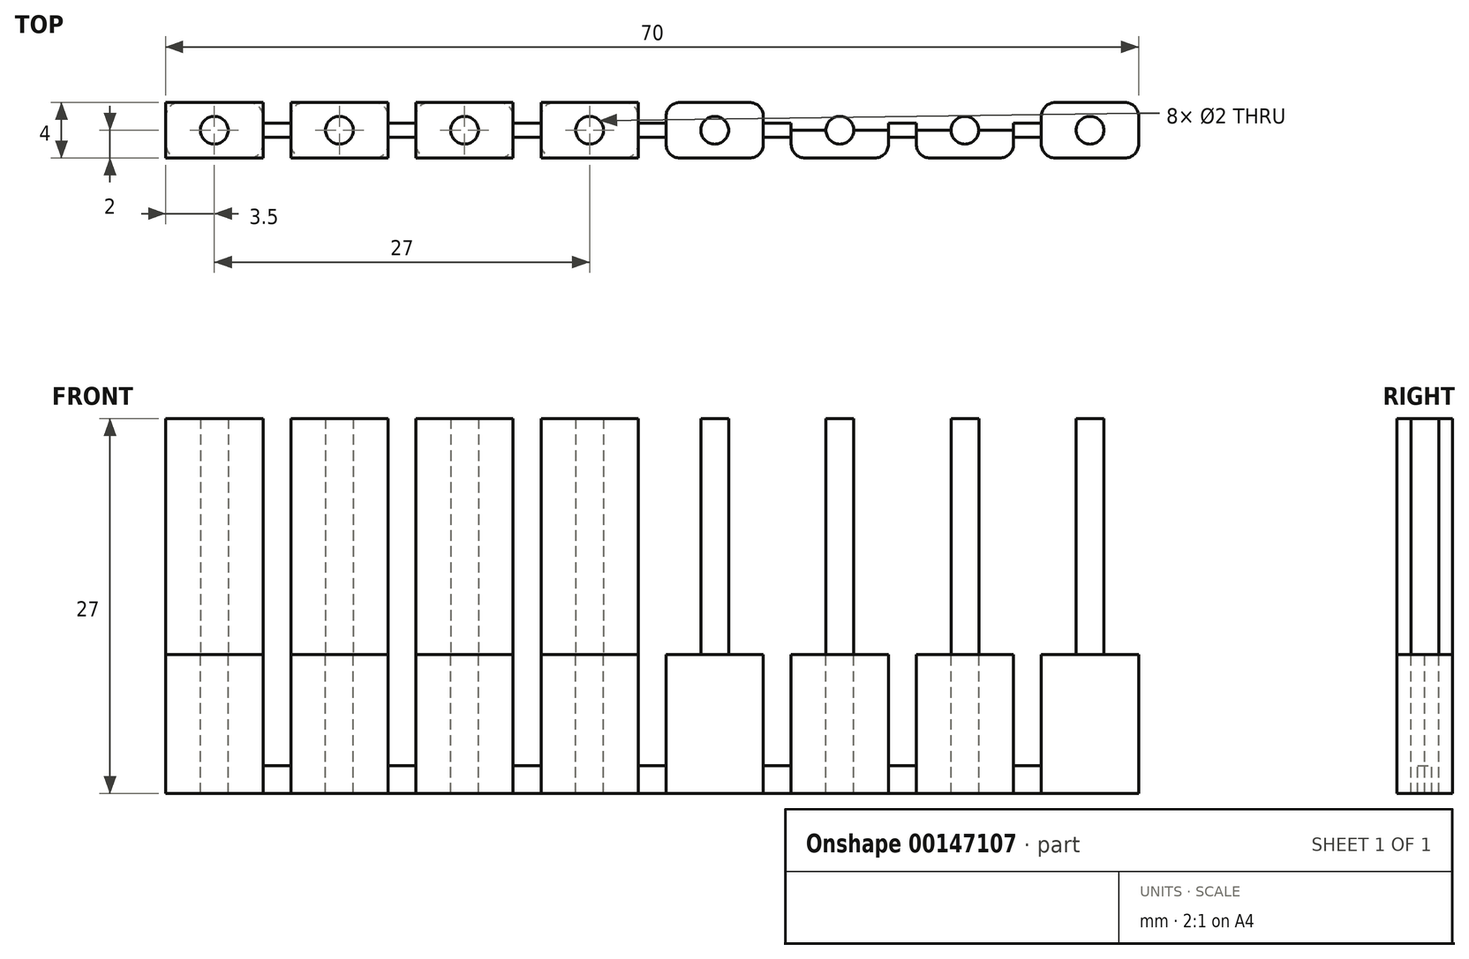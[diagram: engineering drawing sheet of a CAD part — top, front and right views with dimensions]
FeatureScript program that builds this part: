
annotation { "Feature Type Name" : "Feature", "Feature Type Description" : "" }
export const myFeature = defineFeature(function(context is Context, id is Id, definition is map)
    precondition{}
    {
        {
            var Q0;
            Q0=qCreatedBy(makeId("Top.planeOp"),FACE);
            var sketch = newSketch(context, id + "F0", { "sketchPlane" : qUnion([Q0])});
            skLineSegment(sketch, "E0.bottom", {"start": v(35, 2) * mm, "end": v(-35, 2) * mm});
            skLineSegment(sketch, "E0.top", {"start": v(35, -2) * mm, "end": v(-35, -2) * mm});
            skLineSegment(sketch, "E0.left", {"start": v(35, 2) * mm, "end": v(35, -2) * mm});
            skLineSegment(sketch, "E0.right", {"start": v(-35, 2) * mm, "end": v(-35, -2) * mm});
            skPoint(sketch, "E0.middle", {"position": v(0, 0) * mm});
            skLineSegment(sketch, "E1", {"start": v(0, 0) * mm, "end": v(4.5, 0) * mm});
            skLineSegment(sketch, "E2", {"start": v(4.5, 0) * mm, "end": v(13.5, 0) * mm});
            skLineSegment(sketch, "E3", {"start": v(13.5, 0) * mm, "end": v(22.5, 0) * mm});
            skLineSegment(sketch, "E4", {"start": v(22.5, 0) * mm, "end": v(31.5, 0) * mm});
            skCircle(sketch, "E5", {"center": v(4.5, 0) * mm, "radius": 1 * mm});
            skCircle(sketch, "E6", {"center": v(13.5, 0) * mm, "radius": 1 * mm});
            skCircle(sketch, "E7", {"center": v(22.5, 0) * mm, "radius": 1 * mm});
            skCircle(sketch, "E8", {"center": v(31.5, 0) * mm, "radius": 1 * mm});
            skLineSegment(sketch, "E9", {"start": v(0, 2) * mm, "end": v(8, 2) * mm});
            skLineSegment(sketch, "E10", {"start": v(8, 2) * mm, "end": v(10, 2) * mm});
            skLineSegment(sketch, "E11", {"start": v(10, 2) * mm, "end": v(17, 2) * mm});
            skLineSegment(sketch, "E12", {"start": v(17, 2) * mm, "end": v(19, 2) * mm});
            skLineSegment(sketch, "E13", {"start": v(19, 2) * mm, "end": v(26, 2) * mm});
            skLineSegment(sketch, "E14", {"start": v(26, 2) * mm, "end": v(28, 2) * mm});
            skLineSegment(sketch, "E15", {"start": v(8, 2) * mm, "end": v(8, 0.5) * mm});
            skLineSegment(sketch, "E16", {"start": v(8, 0.5) * mm, "end": v(10, 0.5) * mm});
            skLineSegment(sketch, "E17", {"start": v(10, 0.5) * mm, "end": v(10, 2) * mm});
            skLineSegment(sketch, "E18", {"start": v(17, 2) * mm, "end": v(17, 0.5) * mm});
            skLineSegment(sketch, "E19", {"start": v(17, 0.5) * mm, "end": v(19, 0.5) * mm});
            skLineSegment(sketch, "E20", {"start": v(19, 0.5) * mm, "end": v(19, 2) * mm});
            skLineSegment(sketch, "E21", {"start": v(26, 2) * mm, "end": v(26, 0.5) * mm});
            skLineSegment(sketch, "E22", {"start": v(26, 0.5) * mm, "end": v(28, 0.5) * mm});
            skLineSegment(sketch, "E23", {"start": v(28, 0.5) * mm, "end": v(28, 2) * mm});
            skLineSegment(sketch, "E24.MirrorCS", {"start": v(8, -0.5) * mm, "end": v(10, -0.5) * mm});
            skLineSegment(sketch, "E25.MirrorCS", {"start": v(8, -2) * mm, "end": v(8, -0.5) * mm});
            skLineSegment(sketch, "E26.MirrorCS", {"start": v(10, -0.5) * mm, "end": v(10, -2) * mm});
            skLineSegment(sketch, "E27.MirrorCS", {"start": v(17, -2) * mm, "end": v(17, -0.5) * mm});
            skLineSegment(sketch, "E28.MirrorCS", {"start": v(19, -0.5) * mm, "end": v(19, -2) * mm});
            skLineSegment(sketch, "E29.MirrorCS", {"start": v(17, -0.5) * mm, "end": v(19, -0.5) * mm});
            skLineSegment(sketch, "E30.MirrorCS", {"start": v(26, -0.5) * mm, "end": v(28, -0.5) * mm});
            skLineSegment(sketch, "E31.MirrorCS", {"start": v(28, -0.5) * mm, "end": v(28, -2) * mm});
            skLineSegment(sketch, "E32.MirrorCS", {"start": v(26, -2) * mm, "end": v(26, -0.5) * mm});
            skLineSegment(sketch, "E33", {"start": v(10, -0.5) * mm, "end": v(10, 0.5) * mm});
            skLineSegment(sketch, "E34", {"start": v(8, -0.5) * mm, "end": v(8, 0.5) * mm});
            skLineSegment(sketch, "E35", {"start": v(17, -0.5) * mm, "end": v(17, 0.5) * mm});
            skLineSegment(sketch, "E36", {"start": v(19, -0.5) * mm, "end": v(19, 0.5) * mm});
            skLineSegment(sketch, "E37", {"start": v(26, -0.5) * mm, "end": v(26, 0.5) * mm});
            skLineSegment(sketch, "E38", {"start": v(28, -0.5) * mm, "end": v(28, 0.5) * mm});
            skLineSegment(sketch, "E39.MirrorCS", {"start": v(-8, -2) * mm, "end": v(-8, -0.5) * mm});
            skCircle(sketch, "E40.MirrorC", {"center": v(-4.5, 0) * mm, "radius": 1 * mm});
            skLineSegment(sketch, "E41.MirrorCS", {"start": v(-8, 2) * mm, "end": v(-8, 0.5) * mm});
            skLineSegment(sketch, "E42.MirrorCS", {"start": v(-8, 0.5) * mm, "end": v(-10, 0.5) * mm});
            skLineSegment(sketch, "E43.MirrorCS", {"start": v(-10, -0.5) * mm, "end": v(-10, -2) * mm});
            skCircle(sketch, "E44.MirrorC", {"center": v(-13.5, 0) * mm, "radius": 1 * mm});
            skLineSegment(sketch, "E45.MirrorCS", {"start": v(-17, -2) * mm, "end": v(-17, -0.5) * mm});
            skLineSegment(sketch, "E46.MirrorCS", {"start": v(-19, -0.5) * mm, "end": v(-19, -2) * mm});
            skLineSegment(sketch, "E47.MirrorCS", {"start": v(-17, -0.5) * mm, "end": v(-19, -0.5) * mm});
            skLineSegment(sketch, "E48.MirrorCS", {"start": v(-17, 0.5) * mm, "end": v(-19, 0.5) * mm});
            skLineSegment(sketch, "E49.MirrorCS", {"start": v(-19, 0.5) * mm, "end": v(-19, 2) * mm});
            skLineSegment(sketch, "E50.MirrorCS", {"start": v(-17, 2) * mm, "end": v(-17, 0.5) * mm});
            skCircle(sketch, "E51.MirrorC", {"center": v(-22.5, 0) * mm, "radius": 1 * mm});
            skLineSegment(sketch, "E52.MirrorCS", {"start": v(-26, -2) * mm, "end": v(-26, -0.5) * mm});
            skLineSegment(sketch, "E53.MirrorCS", {"start": v(-28, -0.5) * mm, "end": v(-28, -2) * mm});
            skLineSegment(sketch, "E54.MirrorCS", {"start": v(-26, -0.5) * mm, "end": v(-28, -0.5) * mm});
            skLineSegment(sketch, "E55.MirrorCS", {"start": v(-26, 0.5) * mm, "end": v(-28, 0.5) * mm});
            skLineSegment(sketch, "E56.MirrorCS", {"start": v(-28, 0.5) * mm, "end": v(-28, 2) * mm});
            skLineSegment(sketch, "E57.MirrorCS", {"start": v(-26, 2) * mm, "end": v(-26, 0.5) * mm});
            skCircle(sketch, "E58.MirrorC", {"center": v(-31.5, 0) * mm, "radius": 1 * mm});
            skLineSegment(sketch, "E59.MirrorCS", {"start": v(-28, -0.5) * mm, "end": v(-28, 0.5) * mm});
            skLineSegment(sketch, "E60.MirrorCS", {"start": v(-26, -0.5) * mm, "end": v(-26, 0.5) * mm});
            skLineSegment(sketch, "E61.MirrorCS", {"start": v(-19, -0.5) * mm, "end": v(-19, 0.5) * mm});
            skLineSegment(sketch, "E62.MirrorCS", {"start": v(-17, -0.5) * mm, "end": v(-17, 0.5) * mm});
            skLineSegment(sketch, "E63.MirrorCS", {"start": v(-8, -0.5) * mm, "end": v(-8, 0.5) * mm});
            skLineSegment(sketch, "E64.MirrorCS", {"start": v(-10, -0.5) * mm, "end": v(-10, 0.5) * mm});
            skLineSegment(sketch, "E65.MirrorCS", {"start": v(-8, -0.5) * mm, "end": v(-10, -0.5) * mm});
            skLineSegment(sketch, "E66.MirrorCS", {"start": v(-10, 0.5) * mm, "end": v(-10, 2) * mm});
            skLineSegment(sketch, "E67", {"start": v(8, 2) * mm, "end": v(1, 2) * mm});
            skLineSegment(sketch, "E68", {"start": v(1, 2) * mm, "end": v(1, 0.5) * mm});
            skLineSegment(sketch, "E69", {"start": v(1, 0.5) * mm, "end": v(-1, 0.5) * mm});
            skLineSegment(sketch, "E70", {"start": v(-1, 0.5) * mm, "end": v(-1, 2) * mm});
            skLineSegment(sketch, "E71", {"start": v(8, -2) * mm, "end": v(1, -2) * mm});
            skLineSegment(sketch, "E72", {"start": v(1, -2) * mm, "end": v(1, -0.5) * mm});
            skLineSegment(sketch, "E73", {"start": v(1, -0.5) * mm, "end": v(-1, -0.5) * mm});
            skLineSegment(sketch, "E74", {"start": v(-1, -0.5) * mm, "end": v(-1, -2) * mm});
            skLineSegment(sketch, "E75", {"start": v(1, -0.5) * mm, "end": v(1, 0.5) * mm});
            skLineSegment(sketch, "E76", {"start": v(-1, -0.5) * mm, "end": v(-1, 0.5) * mm});
            skSolve(sketch);
        }
        {
            var Q0;
            {var subQ0=sQuery(id+"F0.wireOp",EDGE,"E0.left");Q0=makeQuery(id+"F0.imprint","IMPRINT",FACE,{"disambiguationData":[TD([[makeQuery(id+"F0.imprint","IMPRINT",EDGE,{"derivedFrom":subQ0}),-1.0]])]});}
            var Q1;
            {var subQ6=sQuery(id+"F0.wireOp",EDGE,"E0.right");Q1=makeQuery(id+"F0.imprint","IMPRINT",FACE,{"disambiguationData":[TD([[makeQuery(id+"F0.imprint","IMPRINT",EDGE,{"derivedFrom":subQ6}),1.0]])]});}
            var Q2;
            {var subQ10=sQuery(id+"F0.wireOp",EDGE,"E28.MirrorCS");Q2=makeQuery(id+"F0.imprint","IMPRINT",FACE,{"disambiguationData":[TD([[makeQuery(id+"F0.imprint","IMPRINT",EDGE,{"derivedFrom":subQ10}),1.0]])]});}
            var Q3;
            {var subQ5=sQuery(id+"F0.wireOp",EDGE,"E26.MirrorCS");Q3=makeQuery(id+"F0.imprint","IMPRINT",FACE,{"disambiguationData":[TD([[makeQuery(id+"F0.imprint","IMPRINT",EDGE,{"derivedFrom":subQ5}),1.0]])]});}
            var Q4;
            Q4=makeQuery(id+"F0.imprint","IMPRINT",FACE,{"disambiguationData":[TD([[makeQuery(id+"F0.imprint","IMPRINT",EDGE,{"derivedFrom":sQuery(id+"F0.wireOp",EDGE,"E11")}),-1.0]])]});
            var Q5;
            Q5=makeQuery(id+"F0.imprint","IMPRINT",FACE,{"disambiguationData":[TD([[makeQuery(id+"F0.imprint","IMPRINT",EDGE,{"derivedFrom":sQuery(id+"F0.wireOp",EDGE,"E13")}),-1.0]])]});
            var Q6;
            {var subQ1=sQuery(id+"F0.wireOp",EDGE,"E46.MirrorCS");Q6=makeQuery(id+"F0.imprint","IMPRINT",FACE,{"disambiguationData":[TD([[makeQuery(id+"F0.imprint","IMPRINT",EDGE,{"derivedFrom":subQ1}),-1.0]])]});}
            var Q7;
            {var subQ0=sQuery(id+"F0.wireOp",EDGE,"E43.MirrorCS");Q7=makeQuery(id+"F0.imprint","IMPRINT",FACE,{"disambiguationData":[TD([[makeQuery(id+"F0.imprint","IMPRINT",EDGE,{"derivedFrom":subQ0}),-1.0]])]});}
            var Q8;
            {var subQ2=sQuery(id+"F0.wireOp",EDGE,"E15");Q8=makeQuery(id+"F0.imprint","IMPRINT",FACE,{"disambiguationData":[TD([[makeQuery(id+"F0.imprint","IMPRINT",EDGE,{"derivedFrom":subQ2}),-1.0]])]});}
            var Q9;
            {var subQ0=sQuery(id+"F0.wireOp",EDGE,"E25.MirrorCS");Q9=makeQuery(id+"F0.imprint","IMPRINT",FACE,{"disambiguationData":[TD([[makeQuery(id+"F0.imprint","IMPRINT",EDGE,{"derivedFrom":subQ0}),1.0]])]});}
            var Q10;
            {var subQ0=sQuery(id+"F0.wireOp",EDGE,"E39.MirrorCS");Q10=makeQuery(id+"F0.imprint","IMPRINT",FACE,{"disambiguationData":[TD([[makeQuery(id+"F0.imprint","IMPRINT",EDGE,{"derivedFrom":subQ0}),-1.0]])]});}
            var Q11;
            Q11=makeQuery(id+"F0.imprint","IMPRINT",FACE,{"disambiguationData":[TD([[makeQuery(id+"F0.imprint","IMPRINT",EDGE,{"derivedFrom":sQuery(id+"F0.wireOp",EDGE,"E8")}),1.0]])]});
            var Q12;
            {var subQ0=sQuery(id+"F0.wireOp",EDGE,"E4");var subQ1=sQuery(id+"F0.wireOp",EDGE,"E3");var subQ2=makeQuery(id+"F0.imprint","INTERSECT",VERTEX,{"derivedFrom":[subQ1,subQ0]});Q12=makeQuery(id+"F0.imprint","IMPRINT",FACE,{"disambiguationData":[TD([[makeQuery(id+"F0.imprint","IMPRINT",EDGE,{"disambiguationData":[TD([[subQ2,1.0]])],"derivedFrom":subQ1}),1.0]])]});}
            var Q13;
            {var subQ0=sQuery(id+"F0.wireOp",EDGE,"E3");var subQ1=sQuery(id+"F0.wireOp",EDGE,"E2");var subQ2=makeQuery(id+"F0.imprint","INTERSECT",VERTEX,{"derivedFrom":[subQ1,subQ0]});Q13=makeQuery(id+"F0.imprint","IMPRINT",FACE,{"disambiguationData":[TD([[makeQuery(id+"F0.imprint","IMPRINT",EDGE,{"disambiguationData":[TD([[subQ2,1.0]])],"derivedFrom":subQ1}),1.0]])]});}
            var Q14;
            {var subQ0=sQuery(id+"F0.wireOp",EDGE,"E3");var subQ1=sQuery(id+"F0.wireOp",EDGE,"E2");var subQ2=makeQuery(id+"F0.imprint","INTERSECT",VERTEX,{"derivedFrom":[subQ1,subQ0]});Q14=makeQuery(id+"F0.imprint","IMPRINT",FACE,{"disambiguationData":[TD([[makeQuery(id+"F0.imprint","IMPRINT",EDGE,{"disambiguationData":[TD([[subQ2,1.0]])],"derivedFrom":subQ1}),-1.0]])]});}
            var Q15;
            {var subQ0=sQuery(id+"F0.wireOp",EDGE,"E4");var subQ1=sQuery(id+"F0.wireOp",EDGE,"E3");var subQ2=makeQuery(id+"F0.imprint","INTERSECT",VERTEX,{"derivedFrom":[subQ1,subQ0]});Q15=makeQuery(id+"F0.imprint","IMPRINT",FACE,{"disambiguationData":[TD([[makeQuery(id+"F0.imprint","IMPRINT",EDGE,{"disambiguationData":[TD([[subQ2,1.0]])],"derivedFrom":subQ1}),-1.0]])]});}
            var Q16;
            {var subQ0=sQuery(id+"F0.wireOp",EDGE,"E2");var subQ1=sQuery(id+"F0.wireOp",EDGE,"E1");var subQ2=makeQuery(id+"F0.imprint","INTERSECT",VERTEX,{"derivedFrom":[subQ1,subQ0]});Q16=makeQuery(id+"F0.imprint","IMPRINT",FACE,{"disambiguationData":[TD([[makeQuery(id+"F0.imprint","IMPRINT",EDGE,{"disambiguationData":[TD([[subQ2,1.0]])],"derivedFrom":subQ1}),1.0]])]});}
            var Q17;
            {var subQ0=sQuery(id+"F0.wireOp",EDGE,"E2");var subQ1=sQuery(id+"F0.wireOp",EDGE,"E1");var subQ2=makeQuery(id+"F0.imprint","INTERSECT",VERTEX,{"derivedFrom":[subQ1,subQ0]});Q17=makeQuery(id+"F0.imprint","IMPRINT",FACE,{"disambiguationData":[TD([[makeQuery(id+"F0.imprint","IMPRINT",EDGE,{"disambiguationData":[TD([[subQ2,1.0]])],"derivedFrom":subQ1}),-1.0]])]});}
            var Q18;
            Q18=makeQuery(id+"F0.imprint","IMPRINT",FACE,{"disambiguationData":[TD([[makeQuery(id+"F0.imprint","IMPRINT",EDGE,{"derivedFrom":sQuery(id+"F0.wireOp",EDGE,"E40.MirrorC")}),-1.0]])]});
            var Q19;
            Q19=makeQuery(id+"F0.imprint","IMPRINT",FACE,{"disambiguationData":[TD([[makeQuery(id+"F0.imprint","IMPRINT",EDGE,{"derivedFrom":sQuery(id+"F0.wireOp",EDGE,"E44.MirrorC")}),-1.0]])]});
            var Q20;
            Q20=makeQuery(id+"F0.imprint","IMPRINT",FACE,{"disambiguationData":[TD([[makeQuery(id+"F0.imprint","IMPRINT",EDGE,{"derivedFrom":sQuery(id+"F0.wireOp",EDGE,"E51.MirrorC")}),-1.0]])]});
            var Q21;
            Q21=makeQuery(id+"F0.imprint","IMPRINT",FACE,{"disambiguationData":[TD([[makeQuery(id+"F0.imprint","IMPRINT",EDGE,{"derivedFrom":sQuery(id+"F0.wireOp",EDGE,"E58.MirrorC")}),-1.0]])]});
            extrude(context, id + "F1", {"entities" : qUnion([Q0, Q1, Q2, Q3, Q4, Q5, Q6, Q7, Q8, Q9, Q10, Q11, Q12, Q13, Q14, Q15, Q16, Q17, Q18, Q19, Q20, Q21]), "oppositeDirection" : true, "depth" : 10 * mm});
        }
        {
            var Q0;
            {var subQ5=sQuery(id+"F0.wireOp",EDGE,"E24.MirrorCS");Q0=makeQuery(id+"F0.imprint","IMPRINT",FACE,{"disambiguationData":[TD([[makeQuery(id+"F0.imprint","IMPRINT",EDGE,{"derivedFrom":subQ5}),1.0]])]});}
            var Q1;
            {var subQ5=sQuery(id+"F0.wireOp",EDGE,"E16");Q1=makeQuery(id+"F0.imprint","IMPRINT",FACE,{"disambiguationData":[TD([[makeQuery(id+"F0.imprint","IMPRINT",EDGE,{"derivedFrom":subQ5}),-1.0]])]});}
            var Q2;
            {var subQ5=sQuery(id+"F0.wireOp",EDGE,"E29.MirrorCS");Q2=makeQuery(id+"F0.imprint","IMPRINT",FACE,{"disambiguationData":[TD([[makeQuery(id+"F0.imprint","IMPRINT",EDGE,{"derivedFrom":subQ5}),1.0]])]});}
            var Q3;
            {var subQ5=sQuery(id+"F0.wireOp",EDGE,"E19");Q3=makeQuery(id+"F0.imprint","IMPRINT",FACE,{"disambiguationData":[TD([[makeQuery(id+"F0.imprint","IMPRINT",EDGE,{"derivedFrom":subQ5}),-1.0]])]});}
            var Q4;
            {var subQ5=sQuery(id+"F0.wireOp",EDGE,"E30.MirrorCS");Q4=makeQuery(id+"F0.imprint","IMPRINT",FACE,{"disambiguationData":[TD([[makeQuery(id+"F0.imprint","IMPRINT",EDGE,{"derivedFrom":subQ5}),1.0]])]});}
            var Q5;
            {var subQ5=sQuery(id+"F0.wireOp",EDGE,"E22");Q5=makeQuery(id+"F0.imprint","IMPRINT",FACE,{"disambiguationData":[TD([[makeQuery(id+"F0.imprint","IMPRINT",EDGE,{"derivedFrom":subQ5}),-1.0]])]});}
            var Q6;
            {var subQ1=sQuery(id+"F0.wireOp",EDGE,"E69");Q6=makeQuery(id+"F0.imprint","IMPRINT",FACE,{"disambiguationData":[TD([[makeQuery(id+"F0.imprint","IMPRINT",EDGE,{"derivedFrom":subQ1}),1.0]])]});}
            var Q7;
            Q7=makeQuery(id+"F0.imprint","IMPRINT",FACE,{"disambiguationData":[TD([[makeQuery(id+"F0.imprint","IMPRINT",EDGE,{"derivedFrom":sQuery(id+"F0.wireOp",EDGE,"E42.MirrorCS")}),1.0]])]});
            var Q8;
            Q8=makeQuery(id+"F0.imprint","IMPRINT",FACE,{"disambiguationData":[TD([[makeQuery(id+"F0.imprint","IMPRINT",EDGE,{"derivedFrom":sQuery(id+"F0.wireOp",EDGE,"E47.MirrorCS")}),-1.0]])]});
            var Q9;
            Q9=makeQuery(id+"F0.imprint","IMPRINT",FACE,{"disambiguationData":[TD([[makeQuery(id+"F0.imprint","IMPRINT",EDGE,{"derivedFrom":sQuery(id+"F0.wireOp",EDGE,"E54.MirrorCS")}),-1.0]])]});
            extrude(context, id + "F2", {"entities" : qUnion([Q0, Q1, Q2, Q3, Q4, Q5, Q6, Q7, Q8, Q9]), "oppositeDirection" : true, "depth" : 10 * mm, "hasSecondDirection" : true, "secondDirectionOppositeDirection" : true, "secondDirectionDepth" : 8 * mm});
        }
        {
            var Q0;
            {var subQ0=sQuery(id+"F0.wireOp",EDGE,"E2");var subQ1=sQuery(id+"F0.wireOp",EDGE,"E1");var subQ2=makeQuery(id+"F0.imprint","INTERSECT",VERTEX,{"derivedFrom":[subQ1,subQ0]});Q0=makeQuery(id+"F0.imprint","IMPRINT",FACE,{"disambiguationData":[TD([[makeQuery(id+"F0.imprint","IMPRINT",EDGE,{"disambiguationData":[TD([[subQ2,1.0]])],"derivedFrom":subQ1}),-1.0]])]});}
            var Q1;
            {var subQ0=sQuery(id+"F0.wireOp",EDGE,"E3");var subQ1=sQuery(id+"F0.wireOp",EDGE,"E2");var subQ2=makeQuery(id+"F0.imprint","INTERSECT",VERTEX,{"derivedFrom":[subQ1,subQ0]});Q1=makeQuery(id+"F0.imprint","IMPRINT",FACE,{"disambiguationData":[TD([[makeQuery(id+"F0.imprint","IMPRINT",EDGE,{"disambiguationData":[TD([[subQ2,1.0]])],"derivedFrom":subQ1}),-1.0]])]});}
            var Q2;
            {var subQ0=sQuery(id+"F0.wireOp",EDGE,"E4");var subQ1=sQuery(id+"F0.wireOp",EDGE,"E3");var subQ2=makeQuery(id+"F0.imprint","INTERSECT",VERTEX,{"derivedFrom":[subQ1,subQ0]});Q2=makeQuery(id+"F0.imprint","IMPRINT",FACE,{"disambiguationData":[TD([[makeQuery(id+"F0.imprint","IMPRINT",EDGE,{"disambiguationData":[TD([[subQ2,1.0]])],"derivedFrom":subQ1}),-1.0]])]});}
            var Q3;
            Q3=makeQuery(id+"F0.imprint","IMPRINT",FACE,{"disambiguationData":[TD([[makeQuery(id+"F0.imprint","IMPRINT",EDGE,{"derivedFrom":sQuery(id+"F0.wireOp",EDGE,"E8")}),1.0]])]});
            var Q4;
            {var subQ0=sQuery(id+"F0.wireOp",EDGE,"E4");var subQ1=sQuery(id+"F0.wireOp",EDGE,"E3");var subQ2=makeQuery(id+"F0.imprint","INTERSECT",VERTEX,{"derivedFrom":[subQ1,subQ0]});Q4=makeQuery(id+"F0.imprint","IMPRINT",FACE,{"disambiguationData":[TD([[makeQuery(id+"F0.imprint","IMPRINT",EDGE,{"disambiguationData":[TD([[subQ2,1.0]])],"derivedFrom":subQ1}),1.0]])]});}
            var Q5;
            {var subQ0=sQuery(id+"F0.wireOp",EDGE,"E3");var subQ1=sQuery(id+"F0.wireOp",EDGE,"E2");var subQ2=makeQuery(id+"F0.imprint","INTERSECT",VERTEX,{"derivedFrom":[subQ1,subQ0]});Q5=makeQuery(id+"F0.imprint","IMPRINT",FACE,{"disambiguationData":[TD([[makeQuery(id+"F0.imprint","IMPRINT",EDGE,{"disambiguationData":[TD([[subQ2,1.0]])],"derivedFrom":subQ1}),1.0]])]});}
            var Q6;
            {var subQ0=sQuery(id+"F0.wireOp",EDGE,"E2");var subQ1=sQuery(id+"F0.wireOp",EDGE,"E1");var subQ2=makeQuery(id+"F0.imprint","INTERSECT",VERTEX,{"derivedFrom":[subQ1,subQ0]});Q6=makeQuery(id+"F0.imprint","IMPRINT",FACE,{"disambiguationData":[TD([[makeQuery(id+"F0.imprint","IMPRINT",EDGE,{"disambiguationData":[TD([[subQ2,1.0]])],"derivedFrom":subQ1}),1.0]])]});}
            var Q7;
            Q7=makeQuery(id+"F0.imprint","IMPRINT",FACE,{"disambiguationData":[TD([[makeQuery(id+"F0.imprint","IMPRINT",EDGE,{"derivedFrom":sQuery(id+"F0.wireOp",EDGE,"E40.MirrorC")}),-1.0]])]});
            var Q8;
            Q8=makeQuery(id+"F0.imprint","IMPRINT",FACE,{"disambiguationData":[TD([[makeQuery(id+"F0.imprint","IMPRINT",EDGE,{"derivedFrom":sQuery(id+"F0.wireOp",EDGE,"E44.MirrorC")}),-1.0]])]});
            var Q9;
            Q9=makeQuery(id+"F0.imprint","IMPRINT",FACE,{"disambiguationData":[TD([[makeQuery(id+"F0.imprint","IMPRINT",EDGE,{"derivedFrom":sQuery(id+"F0.wireOp",EDGE,"E51.MirrorC")}),-1.0]])]});
            var Q10;
            Q10=makeQuery(id+"F0.imprint","IMPRINT",FACE,{"disambiguationData":[TD([[makeQuery(id+"F0.imprint","IMPRINT",EDGE,{"derivedFrom":sQuery(id+"F0.wireOp",EDGE,"E58.MirrorC")}),-1.0]])]});
            extrude(context, id + "F3", {"entities" : qUnion([Q0, Q1, Q2, Q3, Q4, Q5, Q6, Q7, Q8, Q9, Q10]), "depth" : 17 * mm});
        }
        {
            var Q0;
            Q0=makeQuery(id+"F1.opExtrude","SWEPT_EDGE",EDGE,{"disambiguationData":[OSD([sQuery(id+"F0.wireOp",EDGE,"E0.bottom"),sQuery(id+"F0.wireOp",EDGE,"E0.left")])]});
            var Q1;
            Q1=makeQuery(id+"F1.opExtrude","SWEPT_EDGE",EDGE,{"disambiguationData":[OSD([sQuery(id+"F0.wireOp",EDGE,"E0.bottom"),sQuery(id+"F0.wireOp",EDGE,"E14"),sQuery(id+"F0.wireOp",EDGE,"E23")])]});
            var Q2;
            Q2=makeQuery(id+"F1.opExtrude","SWEPT_EDGE",EDGE,{"disambiguationData":[OSD([sQuery(id+"F0.wireOp",EDGE,"E0.top"),sQuery(id+"F0.wireOp",EDGE,"E0.left")])]});
            var Q3;
            Q3=makeQuery(id+"F1.opExtrude","SWEPT_EDGE",EDGE,{"disambiguationData":[OSD([sQuery(id+"F0.wireOp",EDGE,"E13"),sQuery(id+"F0.wireOp",EDGE,"E14"),sQuery(id+"F0.wireOp",EDGE,"E21")])]});
            var Q4;
            Q4=makeQuery(id+"F1.opExtrude","SWEPT_EDGE",EDGE,{"disambiguationData":[OSD([sQuery(id+"F0.wireOp",EDGE,"E12"),sQuery(id+"F0.wireOp",EDGE,"E13"),sQuery(id+"F0.wireOp",EDGE,"E20")])]});
            var Q5;
            Q5=makeQuery(id+"F1.opExtrude","SWEPT_EDGE",EDGE,{"disambiguationData":[OSD([sQuery(id+"F0.wireOp",EDGE,"E11"),sQuery(id+"F0.wireOp",EDGE,"E12"),sQuery(id+"F0.wireOp",EDGE,"E18")])]});
            var Q6;
            Q6=makeQuery(id+"F1.opExtrude","SWEPT_EDGE",EDGE,{"disambiguationData":[OSD([sQuery(id+"F0.wireOp",EDGE,"E10"),sQuery(id+"F0.wireOp",EDGE,"E11"),sQuery(id+"F0.wireOp",EDGE,"E17")])]});
            var Q7;
            Q7=makeQuery(id+"F1.opExtrude","SWEPT_EDGE",EDGE,{"disambiguationData":[OSD([sQuery(id+"F0.wireOp",EDGE,"E10"),sQuery(id+"F0.wireOp",EDGE,"E15"),sQuery(id+"F0.wireOp",EDGE,"E67")])]});
            var Q8;
            Q8=makeQuery(id+"F1.opExtrude","SWEPT_EDGE",EDGE,{"disambiguationData":[OSD([sQuery(id+"F0.wireOp",EDGE,"E9"),sQuery(id+"F0.wireOp",EDGE,"E67"),sQuery(id+"F0.wireOp",EDGE,"E68")])]});
            var Q9;
            Q9=makeQuery(id+"F1.opExtrude","SWEPT_EDGE",EDGE,{"disambiguationData":[OSD([sQuery(id+"F0.wireOp",EDGE,"E0.bottom"),sQuery(id+"F0.wireOp",EDGE,"E70")])]});
            var Q10;
            Q10=makeQuery(id+"F1.opExtrude","SWEPT_EDGE",EDGE,{"disambiguationData":[OSD([sQuery(id+"F0.wireOp",EDGE,"E0.bottom"),sQuery(id+"F0.wireOp",EDGE,"E41.MirrorCS")])]});
            var Q11;
            Q11=makeQuery(id+"F1.opExtrude","SWEPT_EDGE",EDGE,{"disambiguationData":[OSD([sQuery(id+"F0.wireOp",EDGE,"E0.bottom"),sQuery(id+"F0.wireOp",EDGE,"E66.MirrorCS")])]});
            var Q12;
            Q12=makeQuery(id+"F1.opExtrude","SWEPT_EDGE",EDGE,{"disambiguationData":[OSD([sQuery(id+"F0.wireOp",EDGE,"E0.bottom"),sQuery(id+"F0.wireOp",EDGE,"E50.MirrorCS")])]});
            var Q13;
            Q13=makeQuery(id+"F1.opExtrude","SWEPT_EDGE",EDGE,{"disambiguationData":[OSD([sQuery(id+"F0.wireOp",EDGE,"E0.bottom"),sQuery(id+"F0.wireOp",EDGE,"E49.MirrorCS")])]});
            var Q14;
            Q14=makeQuery(id+"F1.opExtrude","SWEPT_EDGE",EDGE,{"disambiguationData":[OSD([sQuery(id+"F0.wireOp",EDGE,"E0.bottom"),sQuery(id+"F0.wireOp",EDGE,"E57.MirrorCS")])]});
            var Q15;
            Q15=makeQuery(id+"F1.opExtrude","SWEPT_EDGE",EDGE,{"disambiguationData":[OSD([sQuery(id+"F0.wireOp",EDGE,"E0.bottom"),sQuery(id+"F0.wireOp",EDGE,"E56.MirrorCS")])]});
            var Q16;
            Q16=makeQuery(id+"F1.opExtrude","SWEPT_EDGE",EDGE,{"disambiguationData":[OSD([sQuery(id+"F0.wireOp",EDGE,"E0.bottom"),sQuery(id+"F0.wireOp",EDGE,"E0.right")])]});
            var Q17;
            Q17=makeQuery(id+"F1.opExtrude","SWEPT_EDGE",EDGE,{"disambiguationData":[OSD([sQuery(id+"F0.wireOp",EDGE,"E0.top"),sQuery(id+"F0.wireOp",EDGE,"E31.MirrorCS")])]});
            var Q18;
            Q18=makeQuery(id+"F1.opExtrude","SWEPT_EDGE",EDGE,{"disambiguationData":[OSD([sQuery(id+"F0.wireOp",EDGE,"E0.top"),sQuery(id+"F0.wireOp",EDGE,"E32.MirrorCS")])]});
            var Q19;
            Q19=makeQuery(id+"F1.opExtrude","SWEPT_EDGE",EDGE,{"disambiguationData":[OSD([sQuery(id+"F0.wireOp",EDGE,"E0.top"),sQuery(id+"F0.wireOp",EDGE,"E28.MirrorCS")])]});
            var Q20;
            Q20=makeQuery(id+"F1.opExtrude","SWEPT_EDGE",EDGE,{"disambiguationData":[OSD([sQuery(id+"F0.wireOp",EDGE,"E0.top"),sQuery(id+"F0.wireOp",EDGE,"E27.MirrorCS")])]});
            var Q21;
            Q21=makeQuery(id+"F1.opExtrude","SWEPT_EDGE",EDGE,{"disambiguationData":[OSD([sQuery(id+"F0.wireOp",EDGE,"E0.top"),sQuery(id+"F0.wireOp",EDGE,"E26.MirrorCS")])]});
            var Q22;
            Q22=makeQuery(id+"F1.opExtrude","SWEPT_EDGE",EDGE,{"disambiguationData":[OSD([sQuery(id+"F0.wireOp",EDGE,"E0.top"),sQuery(id+"F0.wireOp",EDGE,"E25.MirrorCS"),sQuery(id+"F0.wireOp",EDGE,"E71")])]});
            var Q23;
            Q23=makeQuery(id+"F1.opExtrude","SWEPT_EDGE",EDGE,{"disambiguationData":[OSD([sQuery(id+"F0.wireOp",EDGE,"E0.top"),sQuery(id+"F0.wireOp",EDGE,"E71"),sQuery(id+"F0.wireOp",EDGE,"E72")])]});
            var Q24;
            Q24=makeQuery(id+"F1.opExtrude","SWEPT_EDGE",EDGE,{"disambiguationData":[OSD([sQuery(id+"F0.wireOp",EDGE,"E0.top"),sQuery(id+"F0.wireOp",EDGE,"E74")])]});
            var Q25;
            Q25=makeQuery(id+"F1.opExtrude","SWEPT_EDGE",EDGE,{"disambiguationData":[OSD([sQuery(id+"F0.wireOp",EDGE,"E0.top"),sQuery(id+"F0.wireOp",EDGE,"E39.MirrorCS")])]});
            var Q26;
            Q26=makeQuery(id+"F1.opExtrude","SWEPT_EDGE",EDGE,{"disambiguationData":[OSD([sQuery(id+"F0.wireOp",EDGE,"E0.top"),sQuery(id+"F0.wireOp",EDGE,"E43.MirrorCS")])]});
            var Q27;
            Q27=makeQuery(id+"F1.opExtrude","SWEPT_EDGE",EDGE,{"disambiguationData":[OSD([sQuery(id+"F0.wireOp",EDGE,"E0.top"),sQuery(id+"F0.wireOp",EDGE,"E45.MirrorCS")])]});
            var Q28;
            Q28=makeQuery(id+"F1.opExtrude","SWEPT_EDGE",EDGE,{"disambiguationData":[OSD([sQuery(id+"F0.wireOp",EDGE,"E0.top"),sQuery(id+"F0.wireOp",EDGE,"E46.MirrorCS")])]});
            var Q29;
            Q29=makeQuery(id+"F1.opExtrude","SWEPT_EDGE",EDGE,{"disambiguationData":[OSD([sQuery(id+"F0.wireOp",EDGE,"E0.top"),sQuery(id+"F0.wireOp",EDGE,"E52.MirrorCS")])]});
            var Q30;
            Q30=makeQuery(id+"F1.opExtrude","SWEPT_EDGE",EDGE,{"disambiguationData":[OSD([sQuery(id+"F0.wireOp",EDGE,"E0.top"),sQuery(id+"F0.wireOp",EDGE,"E53.MirrorCS")])]});
            var Q31;
            Q31=makeQuery(id+"F1.opExtrude","SWEPT_EDGE",EDGE,{"disambiguationData":[OSD([sQuery(id+"F0.wireOp",EDGE,"E0.top"),sQuery(id+"F0.wireOp",EDGE,"E0.right")])]});
            fillet(context, id + "F4", {"entities" : qUnion([Q0, Q1, Q2, Q3, Q4, Q5, Q6, Q7, Q8, Q9, Q10, Q11, Q12, Q13, Q14, Q15, Q16, Q17, Q18, Q19, Q20, Q21, Q22, Q23, Q24, Q25, Q26, Q27, Q28, Q29, Q30, Q31]), "radius" : 1 * mm, "tangentPropagation" : true, "allowEdgeOverflow" : false});
        }
    });
